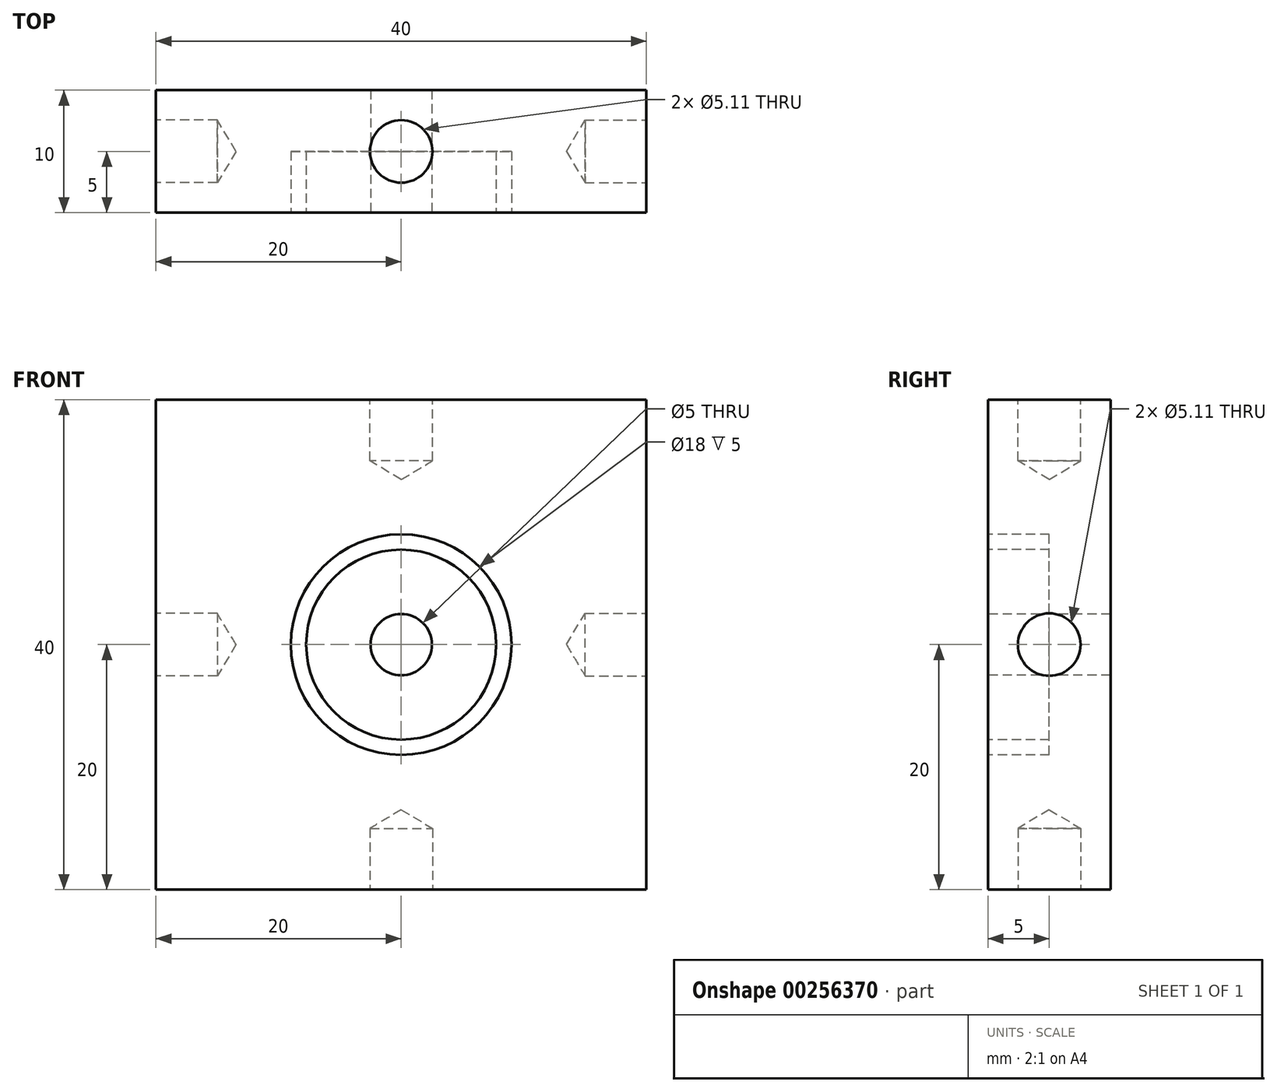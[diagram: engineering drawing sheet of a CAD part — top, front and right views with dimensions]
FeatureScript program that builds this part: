
annotation { "Feature Type Name" : "Feature", "Feature Type Description" : "" }
export const myFeature = defineFeature(function(context is Context, id is Id, definition is map)
    precondition{}
    {
        {
            var Q0;
            Q0=qCreatedBy(makeId("Front.planeOp"),FACE);
            var sketch = newSketch(context, id + "F0", { "sketchPlane" : qUnion([Q0])});
            skLineSegment(sketch, "E0.bottom", {"start": v(-20, 20) * mm, "end": v(20, 20) * mm});
            skLineSegment(sketch, "E0.top", {"start": v(-20, -20) * mm, "end": v(20, -20) * mm});
            skLineSegment(sketch, "E0.left", {"start": v(-20, 20) * mm, "end": v(-20, -20) * mm});
            skLineSegment(sketch, "E0.right", {"start": v(20, 20) * mm, "end": v(20, -20) * mm});
            skSolve(sketch);
        }
        {
            var Q0;
            Q0=makeQuery(id+"F0.imprint","IMPRINT",FACE,{"disambiguationData":[TD([[makeQuery(id+"F0.imprint","IMPRINT",EDGE,{"derivedFrom":sQuery(id+"F0.wireOp",EDGE,"E0.bottom")}),-1.0]])]});
            extrude(context, id + "F1", {"entities" : qUnion([Q0]), "depth" : 10 * mm});
        }
        {
            var Q0;
            Q0=makeQuery(id+"F1.opExtrude","CAP_FACE",FACE,{"disambiguationData":[OSD([sQuery(id+"F0.wireOp",EDGE,"E0.bottom"),sQuery(id+"F0.wireOp",EDGE,"E0.top"),sQuery(id+"F0.wireOp",EDGE,"E0.left"),sQuery(id+"F0.wireOp",EDGE,"E0.right")])],"isStart":false});
            var sketch = newSketch(context, id + "F2", { "sketchPlane" : qUnion([Q0])});
            skPoint(sketch, "E1", {"position": v(0, 0) * mm});
            skSolve(sketch);
        }
        {
            var Q0;
            Q0=sQuery(id+"F2.wireOp",VERTEX,"E1");
            var Q1;
            Q1=makeQuery(id+"F1.opExtrude","SWEPT_BODY",BODY,{"disambiguationData":[OSD([sQuery(id+"F0.wireOp",EDGE,"E0.bottom"),sQuery(id+"F0.wireOp",EDGE,"E0.top"),sQuery(id+"F0.wireOp",EDGE,"E0.left"),sQuery(id+"F0.wireOp",EDGE,"E0.right")])]});
            hole(context, id + "F3", {"style" : HoleStyle.SIMPLE, "endStyle" : HoleEndStyle.THROUGH, "standardTappedOrClearance" : lookupTablePath({ "standard" : "ISO", "size" : "5", "type" : "Drilled" }), "standardBlindInLast" : lookupTablePath({ "standard" : "ISO", "size" : "5", "type" : "Drilled" }), "holeDiameter" : 5 * mm, "tappedDepth" : 12 * mm, "tapClearance" : 3, "locations" : qUnion([Q0]), "scope" : qUnion([Q1])});
        }
        {
            var Q0;
            Q0=makeQuery(id+"F1.opExtrude","CAP_FACE",FACE,{"disambiguationData":[OSD([sQuery(id+"F0.wireOp",EDGE,"E0.bottom"),sQuery(id+"F0.wireOp",EDGE,"E0.top"),sQuery(id+"F0.wireOp",EDGE,"E0.left"),sQuery(id+"F0.wireOp",EDGE,"E0.right")])],"isStart":false});
            var sketch = newSketch(context, id + "F4", { "sketchPlane" : qUnion([Q0])});
            skCircle(sketch, "E2", {"center": v(0, 0) * mm, "radius": 9 * mm});
            skCircle(sketch, "E3", {"center": v(0, 0) * mm, "radius": 7.75 * mm});
            skSolve(sketch);
        }
        {
            var Q0;
            Q0 = qSketchRegion(id + "F4", true);
            extrude(context, id + "F5", {"entities" : qUnion([Q0]), "operationType" : NewBodyOperationType.REMOVE, "oppositeDirection" : true, "depth" : 5 * mm});
        }
        {
            var Q0;
            Q0=makeQuery(id+"F1.opExtrude","SWEPT_FACE",FACE,{"disambiguationData":[OSD([sQuery(id+"F0.wireOp",EDGE,"E0.bottom")])]});
            var sketch = newSketch(context, id + "F6", { "sketchPlane" : qUnion([Q0])});
            skPoint(sketch, "E4", {"position": v(0, -5) * mm});
            skSolve(sketch);
        }
        {
            var Q0;
            Q0=sQuery(id+"F6.wireOp",VERTEX,"E4");
            var Q1;
            Q1=makeQuery(id+"F1.opExtrude","SWEPT_BODY",BODY,{"disambiguationData":[OSD([sQuery(id+"F0.wireOp",EDGE,"E0.bottom"),sQuery(id+"F0.wireOp",EDGE,"E0.top"),sQuery(id+"F0.wireOp",EDGE,"E0.left"),sQuery(id+"F0.wireOp",EDGE,"E0.right")])]});
            hole(context, id + "F7", {"style" : HoleStyle.SIMPLE, "endStyle" : HoleEndStyle.BLIND, "standardTappedOrClearance" : lookupTablePath({ "standard" : "ANSI", "engagement" : "75%", "pitch" : "20 tpi", "size" : "1/4", "type" : "Tapped" }), "standardBlindInLast" : lookupTablePath({ "standard" : "ANSI", "engagement" : "75%", "pitch" : "20 tpi", "size" : "1/4", "type" : "Tapped" }), "holeDiameter" : 5.1 * mm, "showTappedDepth" : true, "holeDepth" : 5 * mm, "isTappedThrough" : true, "tappedDepth" : 1.19 * mm, "tapClearance" : 3, "locations" : qUnion([Q0]), "scope" : qUnion([Q1]), "majorDiameter" : 6.35 * mm});
        }
        {
            var Q0;
            Q0=makeQuery(id+"F1.opExtrude","SWEPT_FACE",FACE,{"disambiguationData":[OSD([sQuery(id+"F0.wireOp",EDGE,"E0.top")])]});
            var sketch = newSketch(context, id + "F8", { "sketchPlane" : qUnion([Q0])});
            skPoint(sketch, "E5", {"position": v(0, 5) * mm});
            skSolve(sketch);
        }
        {
            var Q0;
            Q0=sQuery(id+"F8.wireOp",VERTEX,"E5");
            var Q1;
            Q1=makeQuery(id+"F1.opExtrude","SWEPT_BODY",BODY,{"disambiguationData":[OSD([sQuery(id+"F0.wireOp",EDGE,"E0.bottom"),sQuery(id+"F0.wireOp",EDGE,"E0.top"),sQuery(id+"F0.wireOp",EDGE,"E0.left"),sQuery(id+"F0.wireOp",EDGE,"E0.right")])]});
            hole(context, id + "F9", {"style" : HoleStyle.SIMPLE, "endStyle" : HoleEndStyle.BLIND, "standardTappedOrClearance" : lookupTablePath({ "standard" : "ANSI", "engagement" : "75%", "pitch" : "20 tpi", "size" : "1/4", "type" : "Tapped" }), "standardBlindInLast" : lookupTablePath({ "standard" : "ANSI", "engagement" : "75%", "pitch" : "20 tpi", "size" : "1/4", "type" : "Tapped" }), "holeDiameter" : 5.1 * mm, "showTappedDepth" : true, "holeDepth" : 5 * mm, "isTappedThrough" : true, "tappedDepth" : 1.19 * mm, "tapClearance" : 3, "locations" : qUnion([Q0]), "scope" : qUnion([Q1]), "majorDiameter" : 6.35 * mm});
        }
        {
            var Q0;
            Q0=makeQuery(id+"F1.opExtrude","SWEPT_FACE",FACE,{"disambiguationData":[OSD([sQuery(id+"F0.wireOp",EDGE,"E0.left")])]});
            var sketch = newSketch(context, id + "F10", { "sketchPlane" : qUnion([Q0])});
            skPoint(sketch, "E6", {"position": v(5, 0) * mm});
            skSolve(sketch);
        }
        {
            var Q0;
            Q0=sQuery(id+"F10.wireOp",VERTEX,"E6");
            var Q1;
            Q1=makeQuery(id+"F1.opExtrude","SWEPT_BODY",BODY,{"disambiguationData":[OSD([sQuery(id+"F0.wireOp",EDGE,"E0.bottom"),sQuery(id+"F0.wireOp",EDGE,"E0.top"),sQuery(id+"F0.wireOp",EDGE,"E0.left"),sQuery(id+"F0.wireOp",EDGE,"E0.right")])]});
            hole(context, id + "F11", {"style" : HoleStyle.SIMPLE, "endStyle" : HoleEndStyle.BLIND, "standardTappedOrClearance" : lookupTablePath({ "standard" : "ANSI", "engagement" : "75%", "pitch" : "20 tpi", "size" : "1/4", "type" : "Tapped" }), "standardBlindInLast" : lookupTablePath({ "standard" : "ANSI", "engagement" : "75%", "pitch" : "20 tpi", "size" : "1/4", "type" : "Tapped" }), "holeDiameter" : 5.1 * mm, "showTappedDepth" : true, "holeDepth" : 5 * mm, "isTappedThrough" : true, "tappedDepth" : 1.19 * mm, "tapClearance" : 3, "locations" : qUnion([Q0]), "scope" : qUnion([Q1]), "majorDiameter" : 6.35 * mm});
        }
        {
            var Q0;
            Q0=makeQuery(id+"F1.opExtrude","SWEPT_FACE",FACE,{"disambiguationData":[OSD([sQuery(id+"F0.wireOp",EDGE,"E0.right")])]});
            var sketch = newSketch(context, id + "F12", { "sketchPlane" : qUnion([Q0])});
            skPoint(sketch, "E7", {"position": v(-5, 0) * mm});
            skSolve(sketch);
        }
        {
            var Q0;
            Q0=sQuery(id+"F12.wireOp",VERTEX,"E7");
            var Q1;
            Q1=makeQuery(id+"F1.opExtrude","SWEPT_BODY",BODY,{"disambiguationData":[OSD([sQuery(id+"F0.wireOp",EDGE,"E0.bottom"),sQuery(id+"F0.wireOp",EDGE,"E0.top"),sQuery(id+"F0.wireOp",EDGE,"E0.left"),sQuery(id+"F0.wireOp",EDGE,"E0.right")])]});
            hole(context, id + "F13", {"style" : HoleStyle.SIMPLE, "endStyle" : HoleEndStyle.BLIND, "standardTappedOrClearance" : lookupTablePath({ "standard" : "ANSI", "engagement" : "75%", "pitch" : "20 tpi", "size" : "1/4", "type" : "Tapped" }), "standardBlindInLast" : lookupTablePath({ "standard" : "ANSI", "engagement" : "75%", "pitch" : "20 tpi", "size" : "1/4", "type" : "Tapped" }), "holeDiameter" : 5.1 * mm, "showTappedDepth" : true, "holeDepth" : 5 * mm, "isTappedThrough" : true, "tappedDepth" : 1.19 * mm, "tapClearance" : 3, "locations" : qUnion([Q0]), "scope" : qUnion([Q1]), "majorDiameter" : 6.35 * mm});
        }
    });
